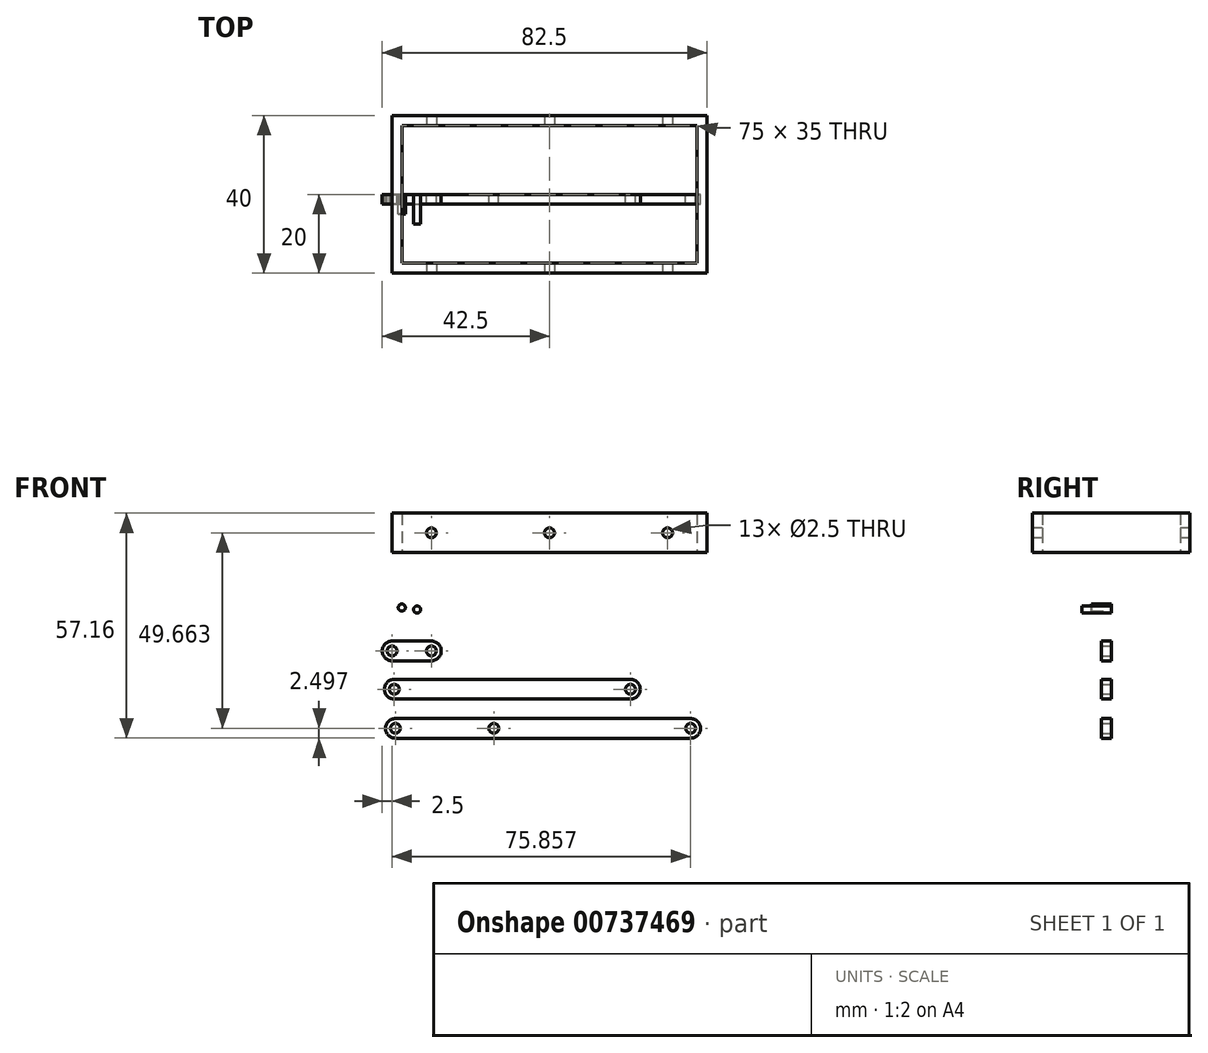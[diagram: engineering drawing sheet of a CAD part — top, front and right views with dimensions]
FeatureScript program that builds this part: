
annotation { "Feature Type Name" : "Feature", "Feature Type Description" : "" }
export const myFeature = defineFeature(function(context is Context, id is Id, definition is map)
    precondition{}
    {
        {
            assignVariable(context, id + "F0", {"name" : "thickness", "anyValue" : 2.5});
        }
        {
            assignVariable(context, id + "F1", {"name" : "pin1", "anyValue" : 5});
        }
        {
            assignVariable(context, id + "F2", {"name" : "pin2", "anyValue" : 7.5});
        }
        {
            var Q0;
            Q0=qCreatedBy(makeId("Front.planeOp"),FACE);
            var sketch = newSketch(context, id + "F3", { "sketchPlane" : qUnion([Q0])});
            skArc(sketch, "E0", {"start": v(0, 2.5) * mm, "mid": v(-2.5, 0) * mm, "end": v(0, -2.5) * mm});
            skArc(sketch, "E1", {"start": v(10, -2.5) * mm, "mid": v(12.5, 0) * mm, "end": v(10, 2.5) * mm});
            skLineSegment(sketch, "E2", {"start": v(0, 2.5) * mm, "end": v(10, 2.5) * mm});
            skLineSegment(sketch, "E3", {"start": v(0, -2.5) * mm, "end": v(10, -2.5) * mm});
            skCircle(sketch, "E4", {"center": v(0, 0) * mm, "radius": 1.25 * mm});
            skCircle(sketch, "E5", {"center": v(10, 0) * mm, "radius": 1.25 * mm});
            skSolve(sketch);
        }
        {
            var Q0;
            Q0=makeQuery(id+"F3.imprint","IMPRINT",FACE,{"disambiguationData":[TD([[makeQuery(id+"F3.imprint","IMPRINT",EDGE,{"derivedFrom":sQuery(id+"F3.wireOp",EDGE,"E0")}),1.0]])]});
            extrude(context, id + "F4", {"entities" : qUnion([Q0]), "depth" : (getVariable(context, 'thickness')) * mm, "offsetDistance" : 25 * mm});
        }
        {
            var Q0;
            Q0=qCreatedBy(makeId("Front.planeOp"),FACE);
            var sketch = newSketch(context, id + "F5", { "sketchPlane" : qUnion([Q0])});
            skArc(sketch, "E6", {"start": v(0.57, -7.23) * mm, "mid": v(-1.93, -9.73) * mm, "end": v(0.57, -12.23) * mm});
            skArc(sketch, "E7", {"start": v(60.57, -12.23) * mm, "mid": v(63.07, -9.73) * mm, "end": v(60.57, -7.23) * mm});
            skLineSegment(sketch, "E8", {"start": v(0.57, -7.23) * mm, "end": v(60.57, -7.23) * mm});
            skLineSegment(sketch, "E9", {"start": v(0.57, -12.23) * mm, "end": v(60.57, -12.23) * mm});
            skCircle(sketch, "E10", {"center": v(0.57, -9.73) * mm, "radius": 1.25 * mm});
            skCircle(sketch, "E11", {"center": v(60.57, -9.73) * mm, "radius": 1.25 * mm});
            skSolve(sketch);
        }
        {
            var Q0;
            Q0=makeQuery(id+"F5.imprint","IMPRINT",FACE,{"disambiguationData":[TD([[makeQuery(id+"F5.imprint","IMPRINT",EDGE,{"derivedFrom":sQuery(id+"F5.wireOp",EDGE,"E6")}),1.0]])]});
            extrude(context, id + "F6", {"entities" : qUnion([Q0]), "depth" : (getVariable(context, 'thickness')) * mm, "offsetDistance" : 25 * mm});
        }
        {
            var Q0;
            Q0=qCreatedBy(makeId("Front.planeOp"),FACE);
            var sketch = newSketch(context, id + "F7", { "sketchPlane" : qUnion([Q0])});
            skArc(sketch, "E12", {"start": v(0.86, -17.16) * mm, "mid": v(-1.64, -19.66) * mm, "end": v(0.86, -22.16) * mm});
            skArc(sketch, "E13", {"start": v(75.86, -22.16) * mm, "mid": v(78.36, -19.66) * mm, "end": v(75.86, -17.16) * mm});
            skLineSegment(sketch, "E14", {"start": v(0.86, -17.16) * mm, "end": v(75.86, -17.16) * mm});
            skLineSegment(sketch, "E15", {"start": v(0.86, -22.16) * mm, "end": v(75.86, -22.16) * mm});
            skCircle(sketch, "E16", {"center": v(0.86, -19.66) * mm, "radius": 1.25 * mm});
            skCircle(sketch, "E17", {"center": v(75.86, -19.66) * mm, "radius": 1.25 * mm});
            skCircle(sketch, "E18", {"center": v(25.86, -19.66) * mm, "radius": 1.25 * mm});
            skSolve(sketch);
        }
        {
            var Q0;
            Q0=makeQuery(id+"F7.imprint","IMPRINT",FACE,{"disambiguationData":[TD([[makeQuery(id+"F7.imprint","IMPRINT",EDGE,{"derivedFrom":sQuery(id+"F7.wireOp",EDGE,"E12")}),1.0]])]});
            extrude(context, id + "F8", {"entities" : qUnion([Q0]), "depth" : (getVariable(context, 'thickness')) * mm, "offsetDistance" : 25 * mm});
        }
        {
            var Q0;
            Q0=qCreatedBy(makeId("Top.planeOp"),FACE);
            cPlane(context, id + "F9", {"entities" : qUnion([Q0]), "cplaneType" : CPlaneType.OFFSET, "offset" : 25 * mm, "width" : 150 * mm, "height" : 150 * mm});
        }
        {
            var Q0;
            Q0=qCreatedBy(id+"F9.planeOp",FACE);
            var sketch = newSketch(context, id + "F10", { "sketchPlane" : qUnion([Q0])});
            skLineSegment(sketch, "E19.bottom", {"start": v(0, 20) * mm, "end": v(80, 20) * mm});
            skLineSegment(sketch, "E19.top", {"start": v(0, -20) * mm, "end": v(80, -20) * mm});
            skLineSegment(sketch, "E19.left", {"start": v(0, 20) * mm, "end": v(0, -20) * mm});
            skLineSegment(sketch, "E19.right", {"start": v(80, 20) * mm, "end": v(80, -20) * mm});
            skLineSegment(sketch, "E20.0", {"start": v(2.5, 17.5) * mm, "end": v(77.5, 17.5) * mm});
            skLineSegment(sketch, "E20.1", {"start": v(2.5, 17.5) * mm, "end": v(2.5, -17.5) * mm});
            skLineSegment(sketch, "E20.2", {"start": v(2.5, -17.5) * mm, "end": v(77.5, -17.5) * mm});
            skLineSegment(sketch, "E20.3", {"start": v(77.5, 17.5) * mm, "end": v(77.5, -17.5) * mm});
            skSolve(sketch);
        }
        {
            var Q0;
            Q0=makeQuery(id+"F10.imprint","IMPRINT",FACE,{"disambiguationData":[TD([[makeQuery(id+"F10.imprint","IMPRINT",EDGE,{"derivedFrom":sQuery(id+"F10.wireOp",EDGE,"E19.bottom")}),-1.0]])]});
            extrude(context, id + "F11", {"entities" : qUnion([Q0]), "depth" : 10 * mm, "offsetDistance" : 25 * mm});
        }
        {
            var Q0;
            Q0=makeQuery(id+"F11.opExtrude","SWEPT_FACE",FACE,{"disambiguationData":[OSD([sQuery(id+"F10.wireOp",EDGE,"E19.top")])]});
            var sketch = newSketch(context, id + "F12", { "sketchPlane" : qUnion([Q0])});
            skCircle(sketch, "E21", {"center": v(10, 30) * mm, "radius": 1.25 * mm});
            skCircle(sketch, "E22", {"center": v(70, 30) * mm, "radius": 1.25 * mm});
            skCircle(sketch, "E23", {"center": v(40, 30) * mm, "radius": 1.25 * mm});
            skPoint(sketch, "E23.centerSnap0", {"position": v(40, 25) * mm});
            skSolve(sketch);
        }
        {
            var Q0;
            Q0=qSketchRegion(id+"F12",true);
            extrude(context, id + "F13", {"entities" : qUnion([Q0]), "operationType" : NewBodyOperationType.REMOVE, "endBound" : BoundingType.THROUGH_ALL, "oppositeDirection" : true, "depth" : 25 * mm, "offsetDistance" : 25 * mm});
        }
        {
            var Q0;
            Q0=qCreatedBy(makeId("Front.planeOp"),FACE);
            var sketch = newSketch(context, id + "F14", { "sketchPlane" : qUnion([Q0])});
            skCircle(sketch, "E24", {"center": v(2.49, 11.02) * mm, "radius": 0.9 * mm});
            skSolve(sketch);
        }
        {
            var Q0;
            Q0=makeQuery(id+"F14.imprint","IMPRINT",FACE,{"disambiguationData":[TD([[makeQuery(id+"F14.imprint","IMPRINT",EDGE,{"derivedFrom":sQuery(id+"F14.wireOp",EDGE,"E24")}),1.0]])]});
            extrude(context, id + "F15", {"entities" : qUnion([Q0]), "depth" : (getVariable(context, 'pin1')) * mm, "offsetDistance" : 25 * mm});
        }
        {
            var Q0;
            Q0=qCreatedBy(makeId("Front.planeOp"),FACE);
            var sketch = newSketch(context, id + "F16", { "sketchPlane" : qUnion([Q0])});
            skCircle(sketch, "E25", {"center": v(6.36, 10.5) * mm, "radius": 0.9 * mm});
            skSolve(sketch);
        }
        {
            var Q0;
            Q0=makeQuery(id+"F16.imprint","IMPRINT",FACE,{"disambiguationData":[TD([[makeQuery(id+"F16.imprint","IMPRINT",EDGE,{"derivedFrom":sQuery(id+"F16.wireOp",EDGE,"E25")}),1.0]])]});
            extrude(context, id + "F17", {"entities" : qUnion([Q0]), "depth" : (getVariable(context, 'pin2')) * mm, "offsetDistance" : 25 * mm});
        }
    });
